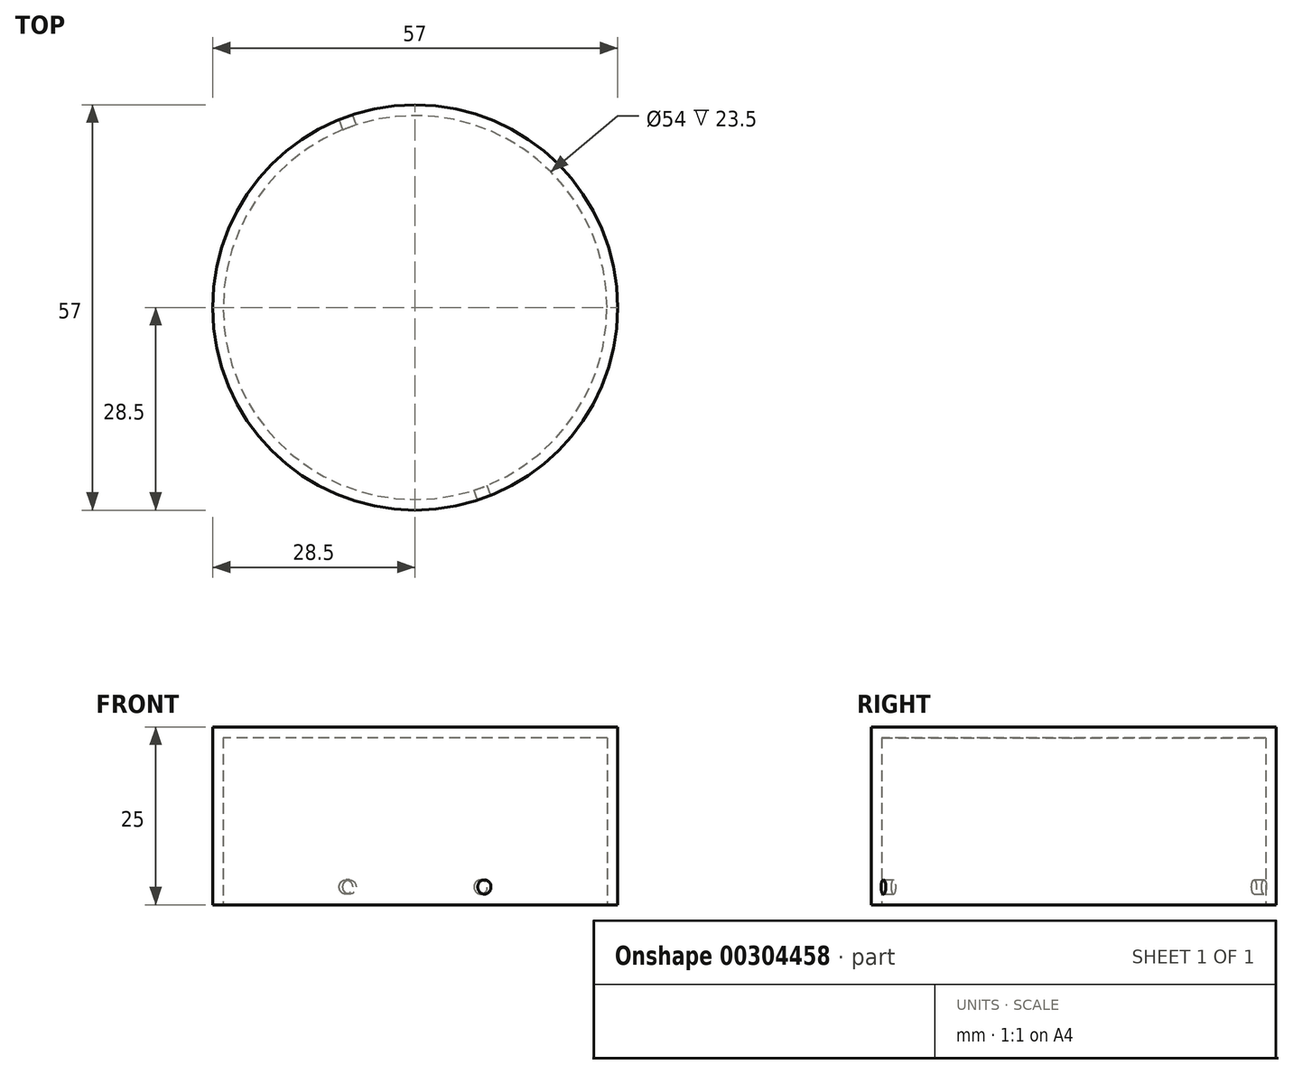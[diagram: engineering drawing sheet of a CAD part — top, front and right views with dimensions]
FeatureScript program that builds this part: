
annotation { "Feature Type Name" : "Feature", "Feature Type Description" : "" }
export const myFeature = defineFeature(function(context is Context, id is Id, definition is map)
    precondition{}
    {
        {
            var Q0;
            Q0=qCreatedBy(makeId("Top.planeOp"),FACE);
            var sketch = newSketch(context, id + "F0", { "sketchPlane" : qUnion([Q0])});
            skCircle(sketch, "E0", {"center": v(0, 0) * mm, "radius": 28.5 * mm});
            skSolve(sketch);
        }
        {
            var Q0;
            Q0 = qSketchRegion(id + "F0", true);
            extrude(context, id + "F1", {"entities" : qUnion([Q0]), "depth" : 25 * mm, "offsetDistance" : 25 * mm});
        }
        {
            var Q0;
            Q0=makeQuery(id+"F1.opExtrude","CAP_FACE",FACE,{"disambiguationData":[OSD([sQuery(id+"F0.wireOp",EDGE,"E0")])],"isStart":true});
            shell(context, id + "F2", {"entities" : qUnion([Q0]), "thickness" : 1.5 * mm});
        }
        {
            var Q0;
            Q0=qCreatedBy(makeId("Top.planeOp"),FACE);
            var sketch = newSketch(context, id + "F3", { "sketchPlane" : qUnion([Q0])});
            skLineSegment(sketch, "E1", {"start": v(0, 21.87) * mm, "end": v(0, -22.9) * mm, "construction": true});
            skLineSegment(sketch, "E2", {"start": v(-9.23, 25.37) * mm, "end": v(10.26, -28.2) * mm, "construction": true});
            skSolve(sketch);
        }
        {
            var Q0;
            Q0=sQuery(id+"F3.wireOp",EDGE,"E2");
            var Q1;
            Q1=sQuery(id+"F3.wireOp",VERTEX,"E2.end");
            cPlane(context, id + "F4", {"entities" : qUnion([Q0, Q1]), "cplaneType" : CPlaneType.CURVE_POINT, "offset" : 25 * mm, "width" : 150 * mm, "height" : 150 * mm});
        }
        {
            var Q0;
            Q0=qCreatedBy(id+"F4.planeOp",FACE);
            var sketch = newSketch(context, id + "F5", { "sketchPlane" : qUnion([Q0])});
            skPoint(sketch, "E3", {"position": v(0, 2.5) * mm});
            skSolve(sketch);
        }
        {
            var Q0;
            Q0=sQuery(id+"F5.wireOp",VERTEX,"E3");
            var Q1;
            Q1=makeQuery(id+"F1.opExtrude","SWEPT_BODY",BODY,{"disambiguationData":[OSD([sQuery(id+"F0.wireOp",EDGE,"E0")])]});
            hole(context, id + "F6", {"style" : HoleStyle.SIMPLE, "endStyle" : HoleEndStyle.THROUGH, "holeDiameter" : 2 * mm, "tappedDepth" : 12 * mm, "tapClearance" : 3, "locations" : qUnion([Q0]), "scope" : qUnion([Q1]), "startStyle" : HoleStartStyle.SKETCH});
        }
    });
